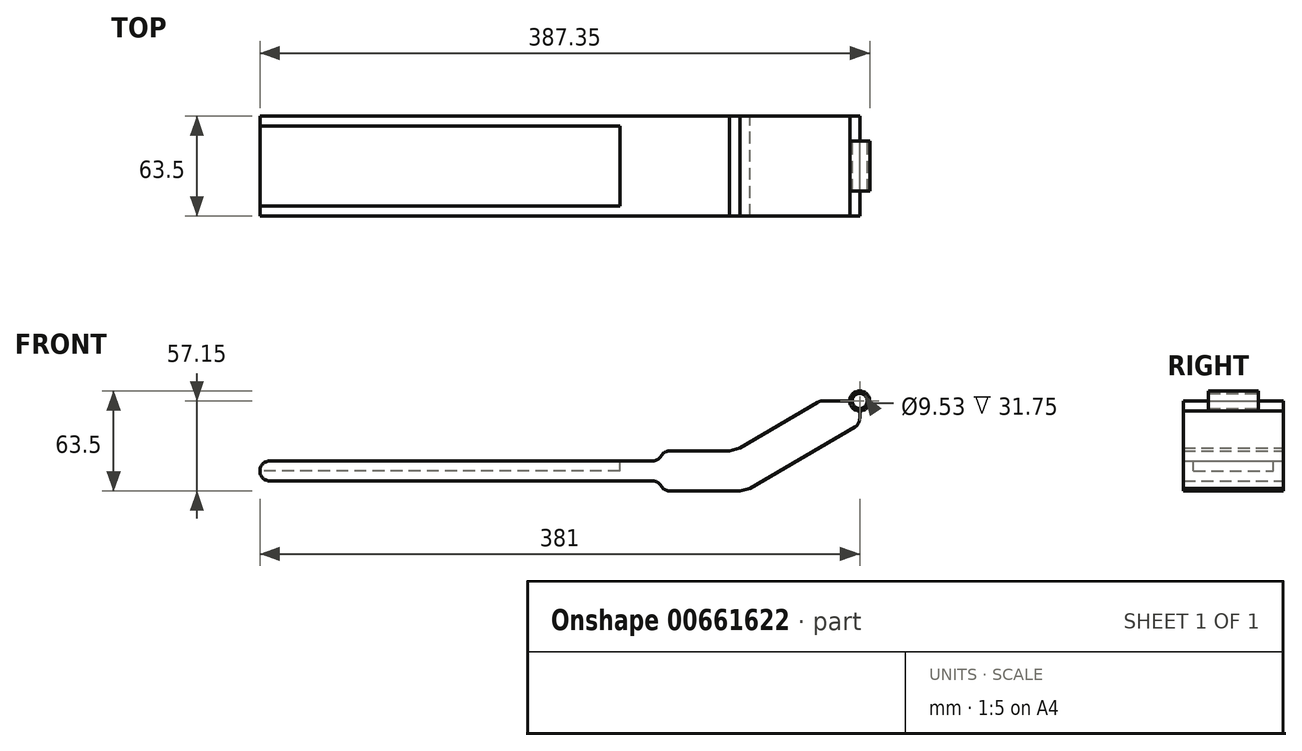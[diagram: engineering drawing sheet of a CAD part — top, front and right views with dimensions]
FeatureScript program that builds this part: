
annotation { "Feature Type Name" : "Feature", "Feature Type Description" : "" }
export const myFeature = defineFeature(function(context is Context, id is Id, definition is map)
    precondition{}
    {
        {
            var Q0;
            Q0=qCreatedBy(makeId("Front.planeOp"),FACE);
            var sketch = newSketch(context, id + "F0", { "sketchPlane" : qUnion([Q0])});
            skLineSegment(sketch, "E0", {"start": v(0, 0) * mm, "end": v(-4.76, 0) * mm});
            skCircle(sketch, "E1", {"center": v(0, 0) * mm, "radius": 4.76 * mm});
            skArc(sketch, "E2", {"start": v(0, -6.35) * mm, "mid": v(4.5, 4.5) * mm, "end": v(-6.35, 0) * mm});
            skLineSegment(sketch, "E3", {"start": v(-355.6, 0) * mm, "end": v(-355.6, -38.1) * mm});
            skLineSegment(sketch, "E4", {"start": v(-152.4, 0) * mm, "end": v(-152.4, -38.1) * mm});
            skLineSegment(sketch, "E5", {"start": v(-152.4, -38.1) * mm, "end": v(-355.6, -38.1) * mm});
            skLineSegment(sketch, "E6", {"start": v(-355.6, -38.1) * mm, "end": v(-374.65, -38.1) * mm});
            skLineSegment(sketch, "E7", {"start": v(-381, -44.45) * mm, "end": v(-381, -44.45) * mm});
            skLineSegment(sketch, "E8", {"start": v(-374.65, -50.8) * mm, "end": v(-131.65, -50.8) * mm});
            skLineSegment(sketch, "E9", {"start": v(-131.65, -38.1) * mm, "end": v(-152.4, -38.1) * mm});
            skLineSegment(sketch, "E10", {"start": v(0, -6.35) * mm, "end": v(0, -11.06) * mm});
            skPoint(sketch, "E10.endSnap0", {"position": v(-127, -44.45) * mm});
            skLineSegment(sketch, "E11.0", {"start": v(-76.2, -57.15) * mm, "end": v(-120.65, -57.15) * mm});
            skLineSegment(sketch, "E12.0", {"start": v(-82.6, -31.75) * mm, "end": v(-120.65, -31.75) * mm});
            skLineSegment(sketch, "E13.0", {"start": v(-76.2, -29.75) * mm, "end": v(-26.69, -0.87) * mm});
            skLineSegment(sketch, "E14.0", {"start": v(-69.8, -55.42) * mm, "end": v(-3.15, -16.54) * mm});
            skLineSegment(sketch, "E15", {"start": v(-127, -38.1) * mm, "end": v(-127, -38.1) * mm});
            skLineSegment(sketch, "E16", {"start": v(-127, -50.8) * mm, "end": v(-127, -50.8) * mm});
            skLineSegment(sketch, "E17", {"start": v(-76.2, -57.15) * mm, "end": v(-69.8, -55.42) * mm});
            skLineSegment(sketch, "E18", {"start": v(-82.6, -31.75) * mm, "end": v(-76.2, -29.75) * mm});
            skPoint(sketch, "E19.orphan", {"position": v(-82.6, -33.48) * mm});
            skPoint(sketch, "E20.orphan", {"position": v(-76.2, -31.75) * mm});
            skPoint(sketch, "E21.orphan", {"position": v(0, -44.45) * mm});
            skPoint(sketch, "E22.visualSharp", {"position": v(-127, -31.75) * mm});
            skArc(sketch, "E22.filletArc", {"start": v(-120.65, -31.75) * mm, "mid": v(-123.83, -32.6) * mm, "end": v(-126.15, -34.92) * mm});
            skPoint(sketch, "E23.visualSharp", {"position": v(-127, -57.15) * mm});
            skArc(sketch, "E23.filletArc", {"start": v(-126.15, -53.98) * mm, "mid": v(-123.82, -56.3) * mm, "end": v(-120.65, -57.15) * mm});
            skPoint(sketch, "E24.visualSharp", {"position": v(-127, -38.1) * mm});
            skArc(sketch, "E24.filletArc", {"start": v(-131.65, -38.1) * mm, "mid": v(-128.47, -37.25) * mm, "end": v(-126.15, -34.93) * mm});
            skPoint(sketch, "E25.visualSharp", {"position": v(-127, -50.8) * mm});
            skArc(sketch, "E25.filletArc", {"start": v(-126.15, -53.98) * mm, "mid": v(-128.47, -51.65) * mm, "end": v(-131.65, -50.8) * mm});
            skPoint(sketch, "E26.visualSharp", {"position": v(-381, -50.8) * mm});
            skArc(sketch, "E26.filletArc", {"start": v(-381, -44.45) * mm, "mid": v(-379.14, -48.94) * mm, "end": v(-374.65, -50.8) * mm});
            skPoint(sketch, "E27.visualSharp", {"position": v(-381, -38.1) * mm});
            skArc(sketch, "E27.filletArc", {"start": v(-374.65, -38.1) * mm, "mid": v(-379.14, -39.96) * mm, "end": v(-381, -44.45) * mm});
            skPoint(sketch, "E28.visualSharp", {"position": v(0, -14.7) * mm});
            skArc(sketch, "E28.filletArc", {"start": v(-3.15, -16.54) * mm, "mid": v(-0.84, -14.22) * mm, "end": v(0, -11.06) * mm});
            skPoint(sketch, "E29.visualSharp", {"position": v(-25.2, 0) * mm});
            skArc(sketch, "E29.filletArc", {"start": v(-23.49, 0) * mm, "mid": v(-25.15, -0.22) * mm, "end": v(-26.69, -0.87) * mm});
            skLineSegment(sketch, "E30.trimOffspring", {"start": v(-6.35, 0) * mm, "end": v(-23.49, 0) * mm});
            skLineSegment(sketch, "E31.trimOffspring", {"start": v(-6.35, 0) * mm, "end": v(-25.2, 0) * mm});
            skLineSegment(sketch, "E32.trimOffspring", {"start": v(-152.4, 0) * mm, "end": v(-220.4, 0) * mm});
            skPoint(sketch, "E33.start.orphan", {"position": v(-381, 0) * mm});
            skArc(sketch, "E34", {"start": v(-278.44, -6.93) * mm, "mid": v(-254, -25.4) * mm, "end": v(-229.56, -6.93) * mm});
            skLineSegment(sketch, "E35.trimOffspring", {"start": v(-287.6, 0) * mm, "end": v(-355.6, 0) * mm});
            skPoint(sketch, "E36.visualSharp", {"position": v(-279.4, 0) * mm});
            skArc(sketch, "E36.filletArc", {"start": v(-278.44, -6.93) * mm, "mid": v(-281.86, -1.93) * mm, "end": v(-287.6, 0) * mm});
            skPoint(sketch, "E37.visualSharp", {"position": v(-228.6, 0) * mm});
            skArc(sketch, "E37.filletArc", {"start": v(-220.4, 0) * mm, "mid": v(-226.14, -1.93) * mm, "end": v(-229.56, -6.93) * mm});
            skSolve(sketch);
        }
        {
            var Q0;
            Q0=makeQuery(id+"F0.imprint","IMPRINT",FACE,{"disambiguationData":[TD([[makeQuery(id+"F0.imprint","IMPRINT",EDGE,{"derivedFrom":sQuery(id+"F0.wireOp",EDGE,"E1")}),-1.0]])]});
            extrude(context, id + "F1", {"entities" : qUnion([Q0]), "depth" : 31.75 * mm, "offsetDistance" : 25.4 * mm, "hasSecondDirection" : true, "secondDirectionOppositeDirection" : true, "secondDirectionDepth" : 31.75 * mm});
        }
        {
            var Q0;
            Q0=qSketchRegion(id+"F0",true);
            extrude(context, id + "F2", {"entities" : qUnion([Q0]), "operationType" : NewBodyOperationType.ADD, "depth" : 25.4 * mm, "offsetDistance" : 25.4 * mm, "hasSecondDirection" : true, "secondDirectionOppositeDirection" : true, "secondDirectionDepth" : 25.4 * mm});
        }
        {
            var Q0;
            Q0=makeQuery(id+"F1.opExtrude","CAP_FACE",FACE,{"disambiguationData":[OSD([sQuery(id+"F0.wireOp",EDGE,"E1"),sQuery(id+"F0.wireOp",EDGE,"E2"),sQuery(id+"F0.wireOp",EDGE,"E5"),sQuery(id+"F0.wireOp",EDGE,"E6"),sQuery(id+"F0.wireOp",EDGE,"E8"),sQuery(id+"F0.wireOp",EDGE,"E9"),sQuery(id+"F0.wireOp",EDGE,"E10"),sQuery(id+"F0.wireOp",EDGE,"E11.0"),sQuery(id+"F0.wireOp",EDGE,"E12.0"),sQuery(id+"F0.wireOp",EDGE,"E13.0"),sQuery(id+"F0.wireOp",EDGE,"E14.0"),sQuery(id+"F0.wireOp",EDGE,"E17"),sQuery(id+"F0.wireOp",EDGE,"E18"),sQuery(id+"F0.wireOp",EDGE,"E22.filletArc"),sQuery(id+"F0.wireOp",EDGE,"E23.filletArc"),sQuery(id+"F0.wireOp",EDGE,"E24.filletArc"),sQuery(id+"F0.wireOp",EDGE,"E25.filletArc"),sQuery(id+"F0.wireOp",EDGE,"E26.filletArc"),sQuery(id+"F0.wireOp",EDGE,"E27.filletArc"),sQuery(id+"F0.wireOp",EDGE,"E28.filletArc"),sQuery(id+"F0.wireOp",EDGE,"E29.filletArc"),sQuery(id+"F0.wireOp",EDGE,"E31.trimOffspring")])],"isStart":false});
            var sketch = newSketch(context, id + "F3", { "sketchPlane" : qUnion([Q0])});
            skCircle(sketch, "E38", {"center": v(0, 0) * mm, "radius": 6.35 * mm});
            skSolve(sketch);
        }
        {
            var Q0;
            Q0=qSketchRegion(id+"F3",true);
            extrude(context, id + "F4", {"entities" : qUnion([Q0]), "operationType" : NewBodyOperationType.REMOVE, "oppositeDirection" : true, "depth" : 15.88 * mm, "offsetDistance" : 25.4 * mm});
        }
        {
            var Q0;
            Q0=makeQuery(id+"F1.opExtrude","CAP_FACE",FACE,{"disambiguationData":[OSD([sQuery(id+"F0.wireOp",EDGE,"E1"),sQuery(id+"F0.wireOp",EDGE,"E2"),sQuery(id+"F0.wireOp",EDGE,"E5"),sQuery(id+"F0.wireOp",EDGE,"E6"),sQuery(id+"F0.wireOp",EDGE,"E8"),sQuery(id+"F0.wireOp",EDGE,"E9"),sQuery(id+"F0.wireOp",EDGE,"E10"),sQuery(id+"F0.wireOp",EDGE,"E11.0"),sQuery(id+"F0.wireOp",EDGE,"E12.0"),sQuery(id+"F0.wireOp",EDGE,"E13.0"),sQuery(id+"F0.wireOp",EDGE,"E14.0"),sQuery(id+"F0.wireOp",EDGE,"E17"),sQuery(id+"F0.wireOp",EDGE,"E18"),sQuery(id+"F0.wireOp",EDGE,"E22.filletArc"),sQuery(id+"F0.wireOp",EDGE,"E23.filletArc"),sQuery(id+"F0.wireOp",EDGE,"E24.filletArc"),sQuery(id+"F0.wireOp",EDGE,"E25.filletArc"),sQuery(id+"F0.wireOp",EDGE,"E26.filletArc"),sQuery(id+"F0.wireOp",EDGE,"E27.filletArc"),sQuery(id+"F0.wireOp",EDGE,"E28.filletArc"),sQuery(id+"F0.wireOp",EDGE,"E29.filletArc"),sQuery(id+"F0.wireOp",EDGE,"E31.trimOffspring")])],"isStart":true});
            var sketch = newSketch(context, id + "F5", { "sketchPlane" : qUnion([Q0])});
            skCircle(sketch, "E39", {"center": v(0, 0) * mm, "radius": 6.35 * mm});
            skSolve(sketch);
        }
        {
            var Q0;
            Q0=qSketchRegion(id+"F5",true);
            extrude(context, id + "F6", {"entities" : qUnion([Q0]), "operationType" : NewBodyOperationType.REMOVE, "oppositeDirection" : true, "depth" : 15.88 * mm, "offsetDistance" : 25.4 * mm});
        }
        {
            var Q0;
            Q0=makeQuery(id+"F2.opExtrude","SWEPT_FACE",FACE,{"disambiguationData":[OSD([sQuery(id+"F0.wireOp",EDGE,"E32.trimOffspring")])]});
            var sketch = newSketch(context, id + "F7", { "sketchPlane" : qUnion([Q0])});
            skLineSegment(sketch, "E40.bottom", {"start": v(-152.4, 25.4) * mm, "end": v(-406.4, 25.4) * mm});
            skLineSegment(sketch, "E40.top", {"start": v(-152.4, -25.4) * mm, "end": v(-406.4, -25.4) * mm});
            skLineSegment(sketch, "E40.left", {"start": v(-152.4, 25.4) * mm, "end": v(-152.4, -25.4) * mm});
            skLineSegment(sketch, "E40.right", {"start": v(-406.4, 25.4) * mm, "end": v(-406.4, -25.4) * mm});
            skSolve(sketch);
        }
        {
            var Q0;
            {var subQ2=sQuery(id+"F7.wireOp",EDGE,"E40.right");Q0=makeQuery(id+"F7.imprint","IMPRINT",FACE,{"disambiguationData":[TD([[makeQuery(id+"F7.imprint","IMPRINT",EDGE,{"derivedFrom":subQ2}),1.0]])]});}
            var Q1;
            {var subQ0=sQuery(id+"F7.wireOp",EDGE,"E40.left");Q1=makeQuery(id+"F7.imprint","IMPRINT",FACE,{"disambiguationData":[TD([[makeQuery(id+"F7.imprint","IMPRINT",EDGE,{"derivedFrom":subQ0}),1.0]])]});}
            extrude(context, id + "F8", {"entities" : qUnion([Q0, Q1]), "operationType" : NewBodyOperationType.REMOVE, "oppositeDirection" : true, "depth" : 44.45 * mm, "offsetDistance" : 25.4 * mm});
        }
    });
